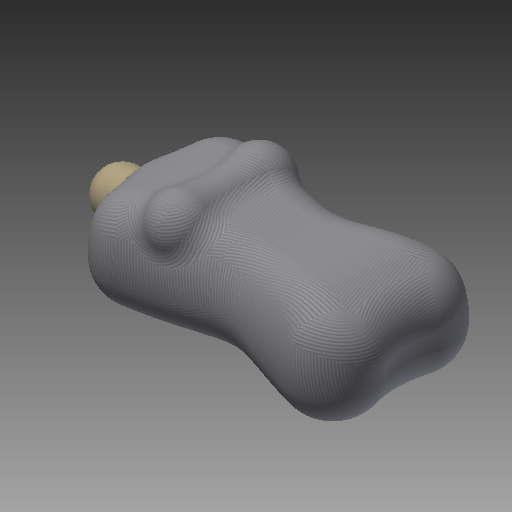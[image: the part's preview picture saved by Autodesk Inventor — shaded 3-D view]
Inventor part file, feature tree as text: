
AUTODESK INVENTOR PART (.ipt)
format: ipt  version: 2022 (Build 260153000, 153)  size: 972,288 bytes
history: native  units: mm (DEFAULTED — no unit token found)
features: other x6, plane x5, sketch x5, revolve x3, fillet x3, extrude x2
ambient origin geometry x8: Origin, YZ Plane, XZ Plane, XY Plane, X Axis, Y Axis, Z Axis, Center Point
bodies: Solid1 (feature_tree)
feature tree (24):
  other  "iMandy - 2D BODY"
  revolve  "Revolution1"  [1 undecoded]
  extrude  "Extrusion3"  Depth=362.458mm
  plane  "Work Plane6"
  extrude  "Extrusion2"  Depth=88.646mm
  plane  "Work Plane7"
  revolve  "Revolution3"  Angle=90.0deg
  fillet  "Fillet1"  Radius=35.4584mm
  fillet  "Fillet3"  Radius=537.00807mm
  plane  "Work Plane2"
  plane  "Work Plane3"
  other  "Work Axis1"
  other  "Work Axis4"
  other  "Work Axis5"
  other  "Work Point5"
  other  "Work Point6"
  plane  "Work Plane9"
  revolve  "Revolution4"  [1 undecoded]
  fillet  "Fillet5"  Radius=107.305623mm
  sketch  "Sketch1"  dims[d1=10.0mm d28=93.296232mm]
  sketch  "Sketch8"  dims[d29=215.9635mm d30=362.458mm]
  sketch  "Sketch9"  dims[d33=13.613568mm d35=88.646mm]
  sketch  "Sketch11"  dims[d36=354.584mm d37=90.0deg d42=35.4584mm d62=537.00807mm]
  sketch  "Sketch14"  dims[d63=158.8008mm d64=-158.8008mm d72=0.0mm d73=107.305623mm d86=25.47239mm d87=0.0mm d88=180.0deg d89=0.0mm d101=164.592mm d102=172.7708mm d103=25.47239mm d104=0.0mm d130=21.27504mm d131=41.148mm d134=43.1927mm d138=10.16mm d139=5.08mm d140=7.62mm d145=38.1mm d146=193.322905mm d149=12.7mm d150=19.05mm d151=6.35mm d152=82.929984mm d153=82.929984mm d154=-85.10016mm d155=63.82512mm d156=276.57552mm d158=177.292mm d159=159.5628mm d160=90.0deg d161=63.82512mm]
note: 2 required parameter values undecoded (feature->parameter linkage not recoverable at this tier; creation-order binding heuristic only, values carry confidence <= 0.55)
